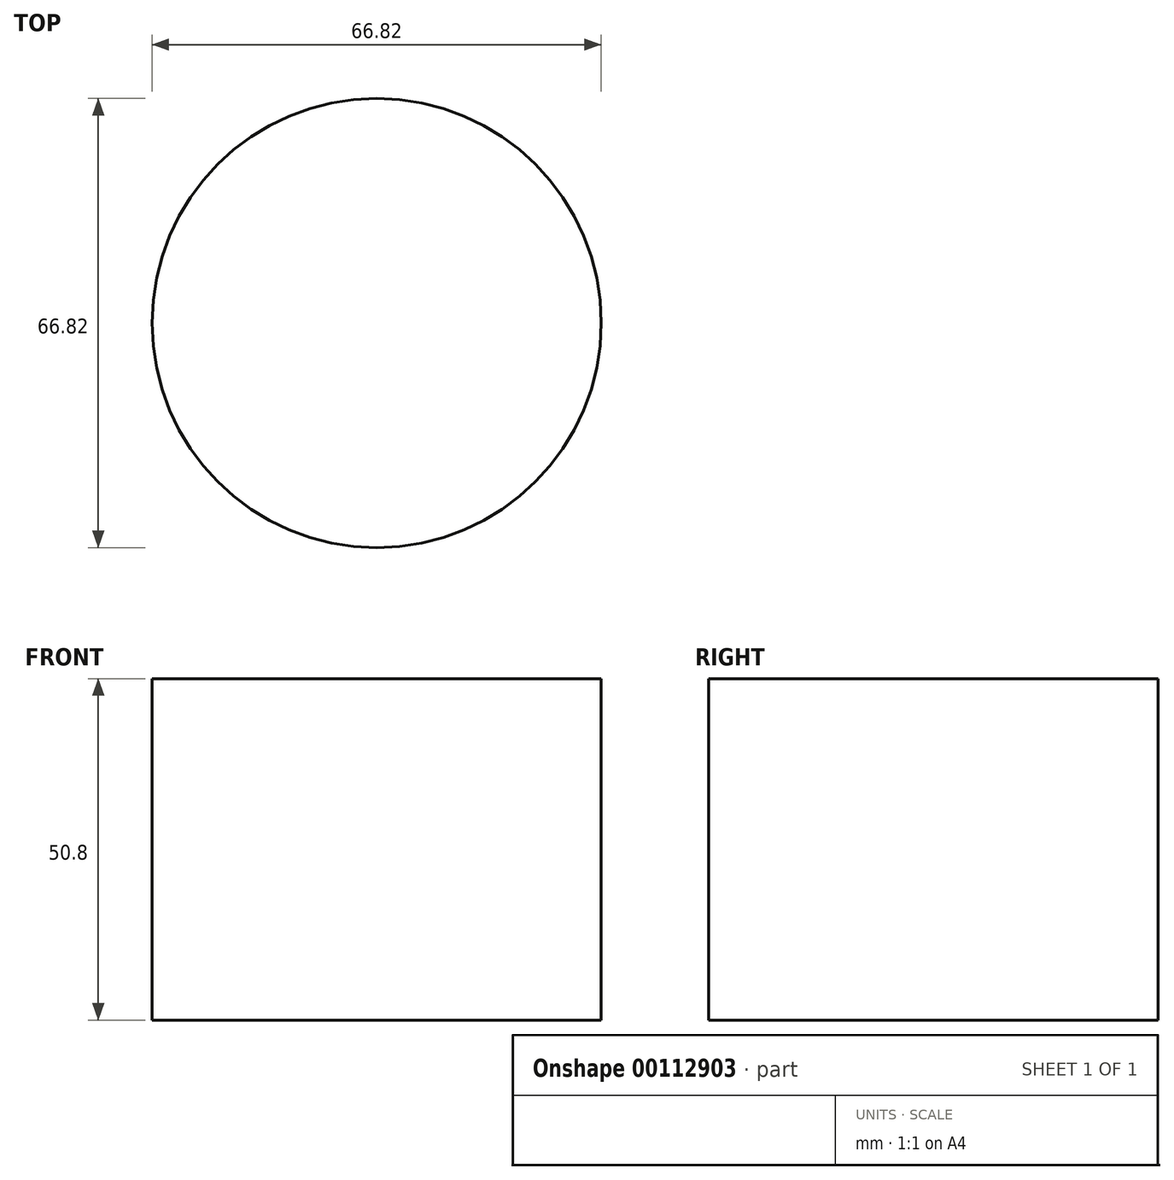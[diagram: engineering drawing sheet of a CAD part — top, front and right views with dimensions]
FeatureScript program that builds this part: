
annotation { "Feature Type Name" : "Feature", "Feature Type Description" : "" }
export const myFeature = defineFeature(function(context is Context, id is Id, definition is map)
    precondition{}
    {
        {
            var Q0;
            Q0=qCreatedBy(makeId("Top.planeOp"),FACE);
            var sketch = newSketch(context, id + "F0", { "sketchPlane" : qUnion([Q0])});
            skCircle(sketch, "E0", {"center": v(0, 0) * mm, "radius": 33.41 * mm});
            skSolve(sketch);
        }
        {
            var Q0;
            Q0=makeQuery(id+"F0.imprint","IMPRINT",FACE,{"disambiguationData":[TD([[makeQuery(id+"F0.imprint","IMPRINT",EDGE,{"derivedFrom":sQuery(id+"F0.wireOp",EDGE,"E0")}),1.0]])]});
            extrude(context, id + "F1", {"entities" : qUnion([Q0]), "endBound" : BoundingType.SYMMETRIC, "depth" : 50.8 * mm});
        }
    });
